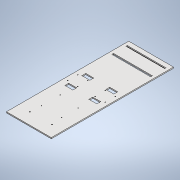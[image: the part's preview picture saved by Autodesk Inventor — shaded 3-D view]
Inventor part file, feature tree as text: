
AUTODESK INVENTOR PART (.ipt)
format: ipt  version: 2020 (Build 240168000, 168)  size: 163,840 bytes
history: native  units: mm
features: reference x14, other x8, extrude x5, sketch x5, mirror x1
ambient origin geometry x8: Origin, YZ Plane, XZ Plane, XY Plane, X Axis, Y Axis, Z Axis, Center Point
bodies: Body1 (feature_tree)
feature tree (33):
  other  "Твердое тело1"
  extrude  "Выдавливание1"  Depth=165.0mm
  extrude  "Выдавливание3"  Depth=450.0mm
  extrude  "Выдавливание4"  Depth=4.0mm TaperAngle=0.0deg
  extrude  "Выдавливание5"  Depth=4.0mm TaperAngle=0.0deg
  mirror  "Зеркальное отражение1"
  extrude  "Выдавливание6"  Depth=4.0mm TaperAngle=0.0deg
  sketch  "Эскиз1"
  sketch  "Эскиз3"
  reference  "Ссылка1"
  reference  "Ссылка2"
  sketch  "Эскиз4"
  reference  "Ссылка3"
  reference  "Ссылка4"
  reference  "Ссылка5"
  reference  "Ссылка6"
  reference  "Ссылка7"
  reference  "Ссылка8"
  reference  "Ссылка9"
  reference  "Ссылка10"
  reference  "Ссылка11"
  reference  "Ссылка12"
  reference  "Ссылка13"
  reference  "Ссылка14"
  sketch  "Эскиз5"
  sketch  "Эскиз6"
  parser-record x1  (decoder bookkeeping rows leaked as tree rows — omitted from the tree; the rows remain in map.json)
  other  "test.iam"
  other  "realsenses_plate_v2.ipt:1"
  other  "realsenses_plate_2:2"
  other  "Odroid_n2:1"
  other  "L298N_V2:2"
  other  "L298N_V2:1"
note: 1 file-system path scrubbed to <path> (originals preserved in map.json)
